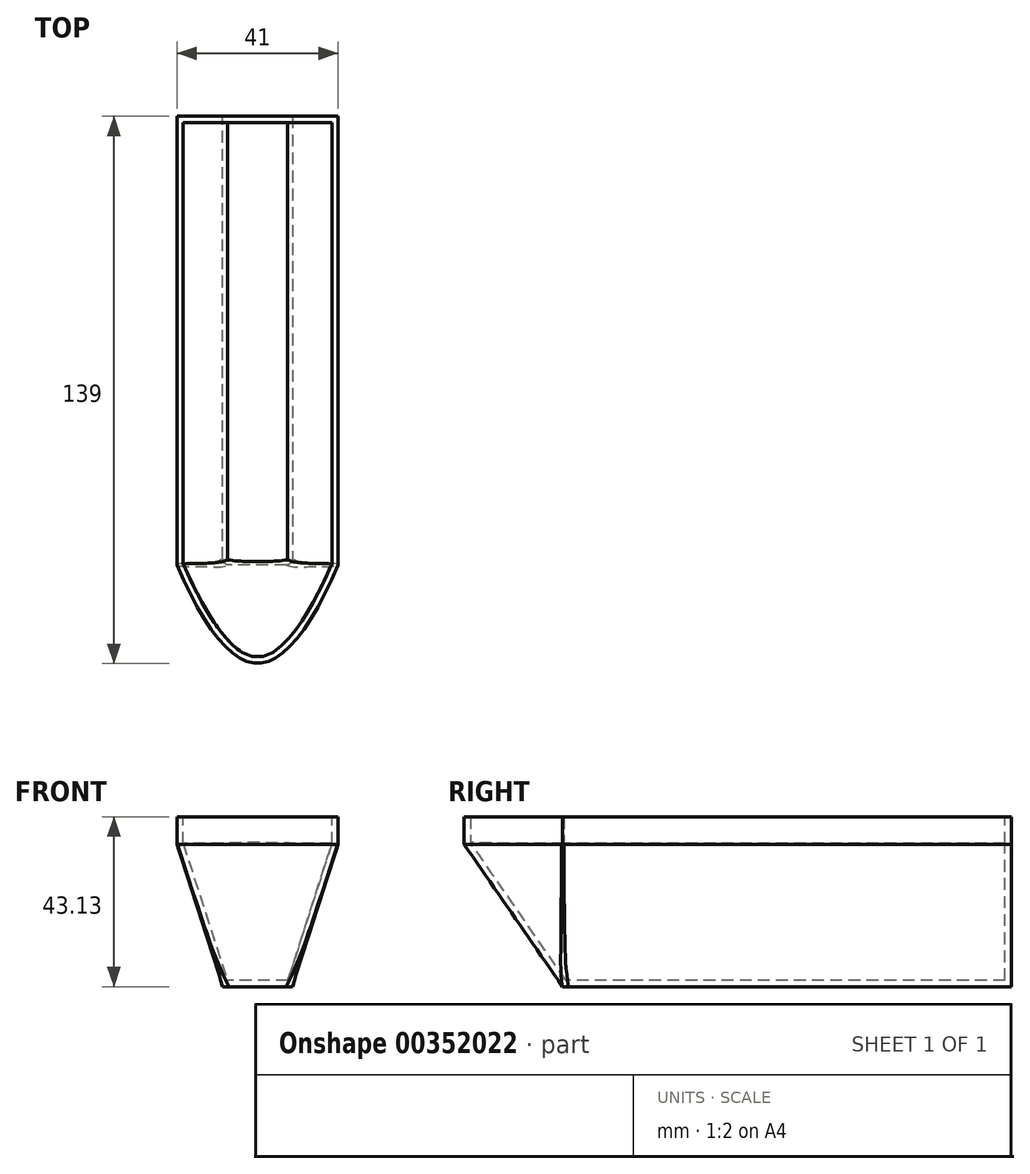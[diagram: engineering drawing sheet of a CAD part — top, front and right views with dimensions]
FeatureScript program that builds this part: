
annotation { "Feature Type Name" : "Feature", "Feature Type Description" : "" }
export const myFeature = defineFeature(function(context is Context, id is Id, definition is map)
    precondition{}
    {
        {
            var Q0;
            Q0=qCreatedBy(makeId("Top.planeOp"),FACE);
            cPlane(context, id + "F0", {"entities" : qUnion([Q0]), "cplaneType" : CPlaneType.OFFSET, "offset" : 36.12 * mm, "width" : 150 * mm, "height" : 150 * mm});
        }
        {
            var Q0;
            Q0=qCreatedBy(id+"F0.planeOp",FACE);
            var sketch = newSketch(context, id + "F1", { "sketchPlane" : qUnion([Q0])});
            skLineSegment(sketch, "E0", {"start": v(20.5, 114) * mm, "end": v(-20.5, 114) * mm});
            skLineSegment(sketch, "E1", {"start": v(20.5, 114) * mm, "end": v(20.5, 0) * mm});
            skLineSegment(sketch, "E2", {"start": v(-20.5, 114) * mm, "end": v(-20.5, 0) * mm});
            skPoint(sketch, "E3", {"position": v(0, -25) * mm});
            skFitSpline(sketch, "E4", {"points": [v(20.5, 0) * mm, v(0, -25) * mm, v(-20.5, 0) * mm], "startDerivative": vector(-39, -90) * mm, "endDerivative": vector(-39, 90) * mm});
            skSolve(sketch);
        }
        {
            var Q0;
            Q0=qCreatedBy(makeId("Top.planeOp"),FACE);
            var sketch = newSketch(context, id + "F2", { "sketchPlane" : qUnion([Q0])});
            skPoint(sketch, "E5", {"position": v(0, 0) * mm});
            skLineSegment(sketch, "E6", {"start": v(-8.83, 114) * mm, "end": v(8.83, 114) * mm});
            skLineSegment(sketch, "E7", {"start": v(8.83, 114) * mm, "end": v(8.83, 0) * mm});
            skLineSegment(sketch, "E8", {"start": v(8.83, 0) * mm, "end": v(-8.83, 0) * mm});
            skLineSegment(sketch, "E9", {"start": v(-8.83, 0) * mm, "end": v(-8.83, 114) * mm});
            skSolve(sketch);
        }
        {
            var Q0;
            Q0=makeQuery(id+"F1.imprint","IMPRINT",FACE,{"disambiguationData":[TD([[makeQuery(id+"F1.imprint","IMPRINT",EDGE,{"derivedFrom":sQuery(id+"F1.wireOp",EDGE,"E0")}),1.0]])]});
            var Q1;
            Q1=makeQuery(id+"F2.imprint","IMPRINT",FACE,{"disambiguationData":[TD([[makeQuery(id+"F2.imprint","IMPRINT",EDGE,{"derivedFrom":sQuery(id+"F2.wireOp",EDGE,"E6")}),-1.0]])]});
            loft(context, id + "F3", {"sheetProfilesArray" : [{ "sheetProfileEntities" : qUnion([Q0]) }, { "sheetProfileEntities" : qUnion([Q1]) }]});
        }
        {
            var Q0;
            Q0=makeQuery(id+"F1.imprint","IMPRINT",FACE,{"disambiguationData":[TD([[makeQuery(id+"F1.imprint","IMPRINT",EDGE,{"derivedFrom":sQuery(id+"F1.wireOp",EDGE,"E0")}),1.0]])]});
            extrude(context, id + "F4", {"entities" : qUnion([Q0]), "operationType" : NewBodyOperationType.ADD, "depth" : 7 * mm});
        }
        {
            var Q0;
            Q0=makeQuery(id+"F4.opExtrude","CAP_FACE",FACE,{"disambiguationData":[OSD([sQuery(id+"F1.wireOp",EDGE,"E0"),sQuery(id+"F1.wireOp",EDGE,"E1"),sQuery(id+"F1.wireOp",EDGE,"E2"),sQuery(id+"F1.wireOp",EDGE,"E4")])],"isStart":false});
            shell(context, id + "F5", {"entities" : qUnion([Q0]), "thickness" : 1.6 * mm});
        }
        {
            var Q0;
            Q0=makeQuery(id+"F3.opLoft","SWEPT_EDGE",EDGE,{"disambiguationData":[OSD([sQuery(id+"F1.wireOp",EDGE,"E1"),sQuery(id+"F1.wireOp",EDGE,"E4"),sQuery(id+"F2.wireOp",EDGE,"E7"),sQuery(id+"F2.wireOp",EDGE,"E8")])]});
            var Q1;
            Q1=makeQuery(id+"F3.opLoft","SWEPT_EDGE",EDGE,{"disambiguationData":[OSD([sQuery(id+"F1.wireOp",EDGE,"E2"),sQuery(id+"F1.wireOp",EDGE,"E4"),sQuery(id+"F2.wireOp",EDGE,"E8"),sQuery(id+"F2.wireOp",EDGE,"E9")])]});
            fillet(context, id + "F6", {"entities" : qUnion([Q0, Q1]), "radius" : 1.6 * mm, "tangentPropagation" : true, "allowEdgeOverflow" : false});
        }
    });
